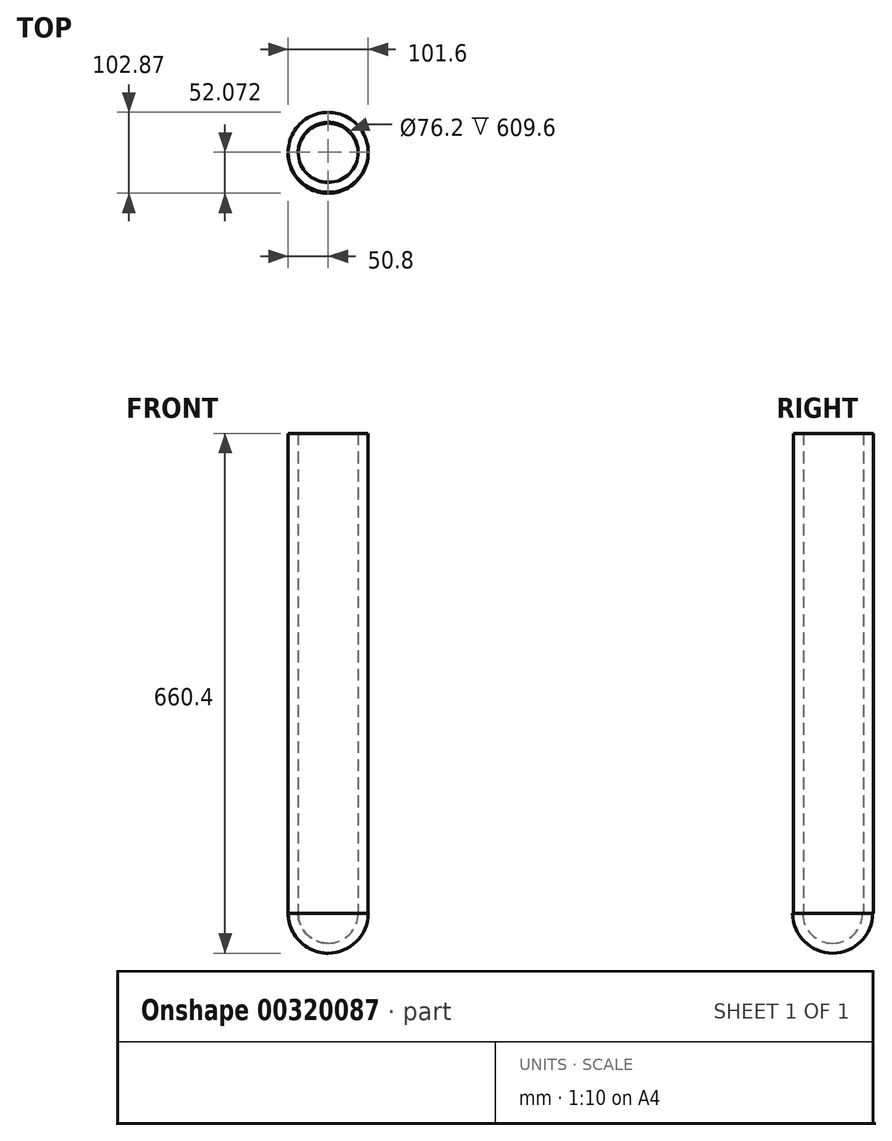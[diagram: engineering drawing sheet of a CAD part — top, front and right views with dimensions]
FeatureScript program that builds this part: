
annotation { "Feature Type Name" : "Feature", "Feature Type Description" : "" }
export const myFeature = defineFeature(function(context is Context, id is Id, definition is map)
    precondition{}
    {
        {
            var Q0;
            Q0=qCreatedBy(makeId("Top.planeOp"),FACE);
            var sketch = newSketch(context, id + "F0", { "sketchPlane" : qUnion([Q0])});
            skCircle(sketch, "E0", {"center": v(0, 1.27) * mm, "radius": 38.1 * mm});
            skCircle(sketch, "E1", {"center": v(0, 1.27) * mm, "radius": 50.8 * mm});
            skSolve(sketch);
        }
        {
            var Q0;
            Q0=makeQuery(id+"F0.imprint","IMPRINT",FACE,{"disambiguationData":[TD([[makeQuery(id+"F0.imprint","IMPRINT",EDGE,{"derivedFrom":sQuery(id+"F0.wireOp",EDGE,"E0")}),-1.0]])]});
            extrude(context, id + "F1", {"entities" : qUnion([Q0]), "depth" : 609.6 * mm});
        }
        {
            var Q0;
            Q0=qCreatedBy(makeId("Front.planeOp"),FACE);
            var sketch = newSketch(context, id + "F2", { "sketchPlane" : qUnion([Q0])});
            skArc(sketch, "E2", {"start": v(-50.8, 0) * mm, "mid": v(-35.92, -35.92) * mm, "end": v(0, -50.8) * mm});
            skArc(sketch, "E3", {"start": v(-38.1, 0) * mm, "mid": v(-26.94, -26.94) * mm, "end": v(0, -38.1) * mm});
            skLineSegment(sketch, "E4", {"start": v(-38.1, 0) * mm, "end": v(-50.8, 0) * mm});
            skLineSegment(sketch, "E5", {"start": v(0, -38.1) * mm, "end": v(0, -50.8) * mm});
            skSolve(sketch);
        }
        {
            var Q0;
            Q0 = qSketchRegion(id + "F2", true);
            var Q1;
            Q1=sQuery(id+"F2.wireOp",EDGE,"E5");
            revolve(context, id + "F3", {"operationType" : NewBodyOperationType.ADD, "entities" : qUnion([Q0]), "axis" : qUnion([Q1]), "revolveType" : RevolveType.FULL});
        }
    });
